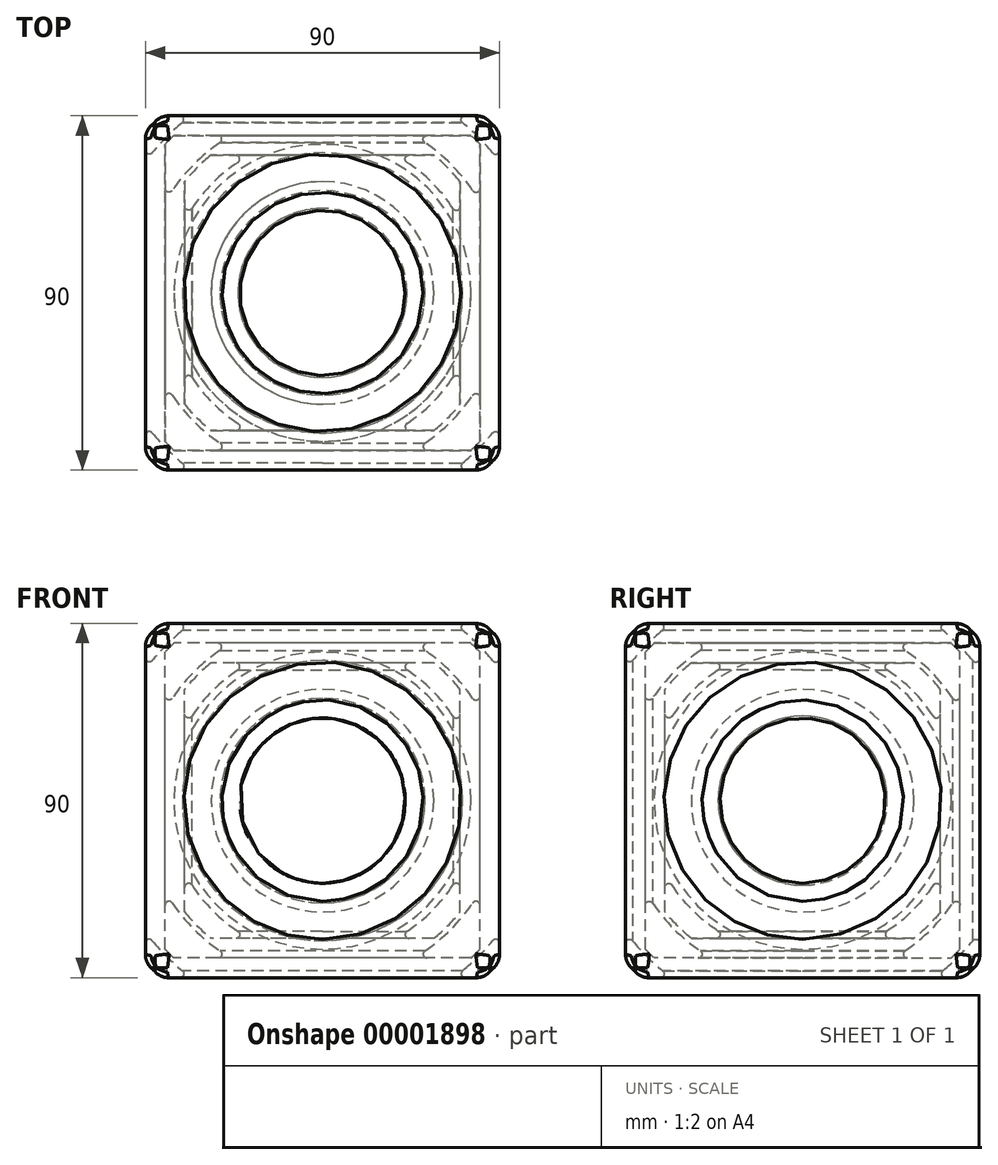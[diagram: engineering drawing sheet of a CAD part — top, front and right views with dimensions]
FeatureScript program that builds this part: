
annotation { "Feature Type Name" : "Feature", "Feature Type Description" : "" }
export const myFeature = defineFeature(function(context is Context, id is Id, definition is map)
    precondition{}
    {
        {
            var Q0;
            Q0=qCreatedBy(makeId("Top.planeOp"),FACE);
            var sketch = newSketch(context, id + "F0", { "sketchPlane" : qUnion([Q0])});
            skLineSegment(sketch, "E0.rect.bottom", {"start": v(35, 35) * mm, "end": v(-35, 35) * mm});
            skLineSegment(sketch, "E0.rect.top", {"start": v(35, -35) * mm, "end": v(-35, -35) * mm});
            skLineSegment(sketch, "E0.rect.left", {"start": v(35, 35) * mm, "end": v(35, -35) * mm});
            skLineSegment(sketch, "E0.rect.right", {"start": v(-35, 35) * mm, "end": v(-35, -35) * mm});
            skPoint(sketch, "E0.rect.middle", {"position": v(0, 0) * mm});
            skSolve(sketch);
        }
        {
            var Q0;
            Q0=qCreatedBy(makeId("Top.planeOp"),FACE);
            var sketch = newSketch(context, id + "F1", { "sketchPlane" : qUnion([Q0])});
            skArc(sketch, "E1", {"start": v(0, 39.5) * mm, "mid": v(-39.5, 0) * mm, "end": v(0, -39.5) * mm});
            skLineSegment(sketch, "E2", {"start": v(0, 39.5) * mm, "end": v(0, -39.5) * mm});
            skSolve(sketch);
        }
        {
            var Q0;
            Q0=makeQuery(id+"F0.imprint","IMPRINT",FACE,{"disambiguationData":[TD([[makeQuery(id+"F0.imprint","IMPRINT",EDGE,{"derivedFrom":sQuery(id+"F0.wireOp",EDGE,"E0.rect.bottom")}),1.0]])]});
            extrude(context, id + "F2", {"entities" : qUnion([Q0]), "endBound" : BoundingType.SYMMETRIC, "depth" : 70 * mm});
        }
        {
            var Q0;
            Q0 = qSketchRegion(id + "F1", true);
            var Q1;
            Q1=sQuery(id+"F1.wireOp",EDGE,"E2");
            revolve(context, id + "F3", {"operationType" : NewBodyOperationType.REMOVE, "entities" : qUnion([Q0]), "axis" : qUnion([Q1]), "revolveType" : RevolveType.FULL, "oppositeDirection" : true});
        }
        {
            var Q0;
            Q0=qCreatedBy(makeId("Top.planeOp"),FACE);
            var sketch = newSketch(context, id + "F4", { "sketchPlane" : qUnion([Q0])});
            skArc(sketch, "E3", {"start": v(0, 45) * mm, "mid": v(-45, 0) * mm, "end": v(0, -45) * mm});
            skLineSegment(sketch, "E4", {"start": v(0, 75) * mm, "end": v(0, -75) * mm});
            skArc(sketch, "E5.0", {"start": v(0, 75) * mm, "mid": v(-75, 0) * mm, "end": v(0, -75) * mm});
            skSolve(sketch);
        }
        {
            var Q0;
            {var subQ2=sQuery(id+"F4.wireOp",EDGE,"E3");Q0=makeQuery(id+"F4.imprint","IMPRINT",FACE,{"disambiguationData":[TD([[makeQuery(id+"F4.imprint","IMPRINT",EDGE,{"derivedFrom":subQ2}),-1.0]])]});}
            var Q1;
            Q1=sQuery(id+"F4.wireOp",EDGE,"E4");
            revolve(context, id + "F5", {"operationType" : NewBodyOperationType.REMOVE, "entities" : qUnion([Q0]), "axis" : qUnion([Q1]), "revolveType" : RevolveType.FULL, "oppositeDirection" : true});
        }
        {
            var Q0;
            Q0=qCreatedBy(makeId("Top.planeOp"),FACE);
            var sketch = newSketch(context, id + "F6", { "sketchPlane" : qUnion([Q0])});
            skLineSegment(sketch, "E6.rect.bottom", {"start": v(40, 40) * mm, "end": v(-40, 40) * mm});
            skLineSegment(sketch, "E6.rect.top", {"start": v(40, -40) * mm, "end": v(-40, -40) * mm});
            skLineSegment(sketch, "E6.rect.left", {"start": v(40, 40) * mm, "end": v(40, -40) * mm});
            skLineSegment(sketch, "E6.rect.right", {"start": v(-40, 40) * mm, "end": v(-40, -40) * mm});
            skPoint(sketch, "E6.rect.middle", {"position": v(0, 0) * mm});
            skSolve(sketch);
        }
        {
            var Q0;
            Q0=qCreatedBy(makeId("Top.planeOp"),FACE);
            var sketch = newSketch(context, id + "F7", { "sketchPlane" : qUnion([Q0])});
            skArc(sketch, "E7", {"start": v(46.2, 0) * mm, "mid": v(0, 46.2) * mm, "end": v(-46.2, 0) * mm});
            skLineSegment(sketch, "E8", {"start": v(-46.2, 0) * mm, "end": v(46.2, 0) * mm});
            skSolve(sketch);
        }
        {
            var Q0;
            Q0=qCreatedBy(makeId("Top.planeOp"),FACE);
            var sketch = newSketch(context, id + "F8", { "sketchPlane" : qUnion([Q0])});
            skArc(sketch, "E9", {"start": v(54.42, 0) * mm, "mid": v(0, 54.42) * mm, "end": v(-54.42, 0) * mm});
            skLineSegment(sketch, "E10", {"start": v(-54.42, 0) * mm, "end": v(54.42, 0) * mm});
            skSolve(sketch);
        }
        {
            var Q0;
            Q0=qCreatedBy(makeId("Top.planeOp"),FACE);
            var sketch = newSketch(context, id + "F9", { "sketchPlane" : qUnion([Q0])});
            skArc(sketch, "E11", {"start": v(55, 0) * mm, "mid": v(0, 55) * mm, "end": v(-55, 0) * mm});
            skLineSegment(sketch, "E12", {"start": v(-111.11, 0) * mm, "end": v(-55, 0) * mm});
            skArc(sketch, "E13.0", {"start": v(111.11, 0) * mm, "mid": v(0, 111.11) * mm, "end": v(-111.11, 0) * mm});
            skLineSegment(sketch, "E14.trimOffspring", {"start": v(55, 0) * mm, "end": v(111.11, 0) * mm});
            skSolve(sketch);
        }
        {
            var Q0;
            Q0=makeQuery(id+"F6.imprint","IMPRINT",FACE,{"disambiguationData":[TD([[makeQuery(id+"F6.imprint","IMPRINT",EDGE,{"derivedFrom":sQuery(id+"F6.wireOp",EDGE,"E6.rect.bottom")}),1.0]])]});
            extrude(context, id + "F10", {"entities" : qUnion([Q0]), "endBound" : BoundingType.SYMMETRIC, "depth" : 80 * mm});
        }
        {
            var Q0;
            Q0 = qSketchRegion(id + "F7", true);
            var Q1;
            Q1=sQuery(id+"F7.wireOp",EDGE,"E7");
            var Q2;
            Q2=sQuery(id+"F8.wireOp",EDGE,"E10");
            revolve(context, id + "F11", {"entities" : qUnion([Q0]), "surfaceEntities" : qUnion([Q1]), "axis" : qUnion([Q2]), "revolveType" : RevolveType.FULL});
        }
        {
            var Q0;
            Q0=makeQuery(id+"F11.opRevolve","SWEPT_BODY",BODY,{"disambiguationData":[OSD([sQuery(id+"F7.wireOp",EDGE,"E7"),sQuery(id+"F7.wireOp",EDGE,"E8")])]});
            var Q1;
            Q1=makeQuery(id+"F10.opExtrude","SWEPT_BODY",BODY,{"disambiguationData":[OSD([sQuery(id+"F6.wireOp",EDGE,"E6.rect.bottom"),sQuery(id+"F6.wireOp",EDGE,"E6.rect.top"),sQuery(id+"F6.wireOp",EDGE,"E6.rect.left"),sQuery(id+"F6.wireOp",EDGE,"E6.rect.right")])]});
            booleanBodies(context, id + "F12", {"operationType" : BooleanOperationType.SUBTRACTION, "tools" : qUnion([Q0]), "targets" : qUnion([Q1])});
        }
        {
            var Q0;
            Q0=makeQuery(id+"F9.imprint","IMPRINT",FACE,{"disambiguationData":[TD([[makeQuery(id+"F9.imprint","IMPRINT",EDGE,{"derivedFrom":sQuery(id+"F9.wireOp",EDGE,"E11")}),-1.0]])]});
            var Q1;
            Q1=sQuery(id+"F9.wireOp",EDGE,"E12");
            revolve(context, id + "F13", {"operationType" : NewBodyOperationType.REMOVE, "entities" : qUnion([Q0]), "axis" : qUnion([Q1]), "revolveType" : RevolveType.FULL, "oppositeDirection" : true});
        }
        {
            var Q0;
            Q0=makeQuery(id+"F12.opBoolean","INTERSECT",EDGE,{"derivedFrom":[makeQuery(id+"F10.opExtrude","CAP_FACE",FACE,{"disambiguationData":[OSD([sQuery(id+"F6.wireOp",EDGE,"E6.rect.bottom"),sQuery(id+"F6.wireOp",EDGE,"E6.rect.top"),sQuery(id+"F6.wireOp",EDGE,"E6.rect.left"),sQuery(id+"F6.wireOp",EDGE,"E6.rect.right")])],"isStart":true}),makeQuery(id+"F11.opRevolve","SWEPT_FACE",FACE,{"disambiguationData":[OSD([sQuery(id+"F7.wireOp",EDGE,"E7")])]})]});
            var Q1;
            Q1=makeQuery(id+"F12.opBoolean","INTERSECT",EDGE,{"derivedFrom":[makeQuery(id+"F10.opExtrude","SWEPT_FACE",FACE,{"disambiguationData":[OSD([sQuery(id+"F6.wireOp",EDGE,"E6.rect.bottom")])]}),makeQuery(id+"F11.opRevolve","SWEPT_FACE",FACE,{"disambiguationData":[OSD([sQuery(id+"F7.wireOp",EDGE,"E7")])]})]});
            var Q2;
            Q2=makeQuery(id+"F12.opBoolean","INTERSECT",EDGE,{"derivedFrom":[makeQuery(id+"F10.opExtrude","SWEPT_FACE",FACE,{"disambiguationData":[OSD([sQuery(id+"F6.wireOp",EDGE,"E6.rect.left")])]}),makeQuery(id+"F11.opRevolve","SWEPT_FACE",FACE,{"disambiguationData":[OSD([sQuery(id+"F7.wireOp",EDGE,"E7")])]})]});
            var Q3;
            Q3=makeQuery(id+"F12.opBoolean","INTERSECT",EDGE,{"derivedFrom":[makeQuery(id+"F10.opExtrude","SWEPT_FACE",FACE,{"disambiguationData":[OSD([sQuery(id+"F6.wireOp",EDGE,"E6.rect.right")])]}),makeQuery(id+"F11.opRevolve","SWEPT_FACE",FACE,{"disambiguationData":[OSD([sQuery(id+"F7.wireOp",EDGE,"E7")])]})]});
            var Q4;
            Q4=makeQuery(id+"F12.opBoolean","INTERSECT",EDGE,{"derivedFrom":[makeQuery(id+"F10.opExtrude","SWEPT_FACE",FACE,{"disambiguationData":[OSD([sQuery(id+"F6.wireOp",EDGE,"E6.rect.top")])]}),makeQuery(id+"F11.opRevolve","SWEPT_FACE",FACE,{"disambiguationData":[OSD([sQuery(id+"F7.wireOp",EDGE,"E7")])]})]});
            var Q5;
            Q5=makeQuery(id+"F12.opBoolean","INTERSECT",EDGE,{"derivedFrom":[makeQuery(id+"F10.opExtrude","CAP_FACE",FACE,{"disambiguationData":[OSD([sQuery(id+"F6.wireOp",EDGE,"E6.rect.bottom"),sQuery(id+"F6.wireOp",EDGE,"E6.rect.top"),sQuery(id+"F6.wireOp",EDGE,"E6.rect.left"),sQuery(id+"F6.wireOp",EDGE,"E6.rect.right")])],"isStart":false}),makeQuery(id+"F11.opRevolve","SWEPT_FACE",FACE,{"disambiguationData":[OSD([sQuery(id+"F7.wireOp",EDGE,"E7")])]})]});
            fillet(context, id + "F14", {"entities" : qUnion([Q0, Q1, Q2, Q3, Q4, Q5]), "radius" : 1 * mm, "tangentPropagation" : true, "allowEdgeOverflow" : false});
        }
        {
            var Q0;
            Q0=makeQuery(id+"F3.boolean.opBoolean","INTERSECT",EDGE,{"derivedFrom":[makeQuery(id+"F2.opExtrude","CAP_FACE",FACE,{"disambiguationData":[OSD([sQuery(id+"F0.wireOp",EDGE,"E0.rect.bottom"),sQuery(id+"F0.wireOp",EDGE,"E0.rect.top"),sQuery(id+"F0.wireOp",EDGE,"E0.rect.left"),sQuery(id+"F0.wireOp",EDGE,"E0.rect.right")])],"isStart":false}),makeQuery(id+"F3.opRevolve","SWEPT_FACE",FACE,{"disambiguationData":[OSD([sQuery(id+"F1.wireOp",EDGE,"E1")])]})]});
            var Q1;
            Q1=makeQuery(id+"F3.boolean.opBoolean","INTERSECT",EDGE,{"derivedFrom":[makeQuery(id+"F2.opExtrude","SWEPT_FACE",FACE,{"disambiguationData":[OSD([sQuery(id+"F0.wireOp",EDGE,"E0.rect.top")])]}),makeQuery(id+"F3.opRevolve","SWEPT_FACE",FACE,{"disambiguationData":[OSD([sQuery(id+"F1.wireOp",EDGE,"E1")])]})]});
            var Q2;
            Q2=makeQuery(id+"F3.boolean.opBoolean","INTERSECT",EDGE,{"derivedFrom":[makeQuery(id+"F2.opExtrude","CAP_FACE",FACE,{"disambiguationData":[OSD([sQuery(id+"F0.wireOp",EDGE,"E0.rect.bottom"),sQuery(id+"F0.wireOp",EDGE,"E0.rect.top"),sQuery(id+"F0.wireOp",EDGE,"E0.rect.left"),sQuery(id+"F0.wireOp",EDGE,"E0.rect.right")])],"isStart":true}),makeQuery(id+"F3.opRevolve","SWEPT_FACE",FACE,{"disambiguationData":[OSD([sQuery(id+"F1.wireOp",EDGE,"E1")])]})]});
            var Q3;
            Q3=makeQuery(id+"F3.boolean.opBoolean","INTERSECT",EDGE,{"derivedFrom":[makeQuery(id+"F2.opExtrude","SWEPT_FACE",FACE,{"disambiguationData":[OSD([sQuery(id+"F0.wireOp",EDGE,"E0.rect.left")])]}),makeQuery(id+"F3.opRevolve","SWEPT_FACE",FACE,{"disambiguationData":[OSD([sQuery(id+"F1.wireOp",EDGE,"E1")])]})]});
            var Q4;
            Q4=makeQuery(id+"F3.boolean.opBoolean","INTERSECT",EDGE,{"derivedFrom":[makeQuery(id+"F2.opExtrude","SWEPT_FACE",FACE,{"disambiguationData":[OSD([sQuery(id+"F0.wireOp",EDGE,"E0.rect.bottom")])]}),makeQuery(id+"F3.opRevolve","SWEPT_FACE",FACE,{"disambiguationData":[OSD([sQuery(id+"F1.wireOp",EDGE,"E1")])]})]});
            var Q5;
            Q5=makeQuery(id+"F3.boolean.opBoolean","INTERSECT",EDGE,{"derivedFrom":[makeQuery(id+"F2.opExtrude","SWEPT_FACE",FACE,{"disambiguationData":[OSD([sQuery(id+"F0.wireOp",EDGE,"E0.rect.right")])]}),makeQuery(id+"F3.opRevolve","SWEPT_FACE",FACE,{"disambiguationData":[OSD([sQuery(id+"F1.wireOp",EDGE,"E1")])]})]});
            fillet(context, id + "F15", {"entities" : qUnion([Q0, Q1, Q2, Q3, Q4, Q5]), "radius" : 1 * mm, "tangentPropagation" : true, "allowEdgeOverflow" : false});
        }
        {
            var Q0;
            Q0=makeQuery(id+"F2.opExtrude","CAP_FACE",FACE,{"disambiguationData":[OSD([sQuery(id+"F0.wireOp",EDGE,"E0.rect.bottom"),sQuery(id+"F0.wireOp",EDGE,"E0.rect.top"),sQuery(id+"F0.wireOp",EDGE,"E0.rect.left"),sQuery(id+"F0.wireOp",EDGE,"E0.rect.right")])],"isStart":true});
            var sketch = newSketch(context, id + "F16", { "sketchPlane" : qUnion([Q0])});
            skCircle(sketch, "E15", {"center": v(0, 0) * mm, "radius": 24 * mm});
            skCircle(sketch, "E16.0", {"center": v(0, 0) * mm, "radius": 23.6 * mm});
            skSolve(sketch);
        }
        {
            var Q0;
            Q0=qCreatedBy(makeId("Top.planeOp"),FACE);
            var sketch = newSketch(context, id + "F17", { "sketchPlane" : qUnion([Q0])});
            skLineSegment(sketch, "E17.rect.bottom", {"start": v(45, 45) * mm, "end": v(-45, 45) * mm});
            skLineSegment(sketch, "E17.rect.top", {"start": v(45, -45) * mm, "end": v(-45, -45) * mm});
            skLineSegment(sketch, "E17.rect.left", {"start": v(45, 45) * mm, "end": v(45, -45) * mm});
            skLineSegment(sketch, "E17.rect.right", {"start": v(-45, 45) * mm, "end": v(-45, -45) * mm});
            skPoint(sketch, "E17.rect.middle", {"position": v(0, 0) * mm});
            skSolve(sketch);
        }
        {
            var Q0;
            Q0=qCreatedBy(makeId("Top.planeOp"),FACE);
            var sketch = newSketch(context, id + "F18", { "sketchPlane" : qUnion([Q0])});
            skArc(sketch, "E18", {"start": v(56, 0) * mm, "mid": v(0, 56) * mm, "end": v(-56, 0) * mm});
            skLineSegment(sketch, "E19", {"start": v(-56, 0) * mm, "end": v(56, 0) * mm});
            skSolve(sketch);
        }
        {
            var Q0;
            Q0=makeQuery(id+"F17.imprint","IMPRINT",FACE,{"disambiguationData":[TD([[makeQuery(id+"F17.imprint","IMPRINT",EDGE,{"derivedFrom":sQuery(id+"F17.wireOp",EDGE,"E17.rect.bottom")}),1.0]])]});
            var Q1;
            Q1 = qSketchRegion(id + "F16", true);
            extrude(context, id + "F19", {"entities" : qUnion([Q0, Q1]), "endBound" : BoundingType.SYMMETRIC, "depth" : 90 * mm});
        }
        {
            var Q0;
            Q0 = qSketchRegion(id + "F18", true);
            var Q1;
            Q1=sQuery(id+"F18.wireOp",EDGE,"E19");
            revolve(context, id + "F20", {"entities" : qUnion([Q0]), "axis" : qUnion([Q1]), "revolveType" : RevolveType.FULL});
        }
        {
            var Q0;
            Q0=makeQuery(id+"F20.opRevolve","SWEPT_BODY",BODY,{"disambiguationData":[OSD([sQuery(id+"F18.wireOp",EDGE,"E18"),sQuery(id+"F18.wireOp",EDGE,"E19")])]});
            var Q1;
            Q1=makeQuery(id+"F19.opExtrude","SWEPT_BODY",BODY,{"disambiguationData":[OSD([sQuery(id+"F17.wireOp",EDGE,"E17.rect.bottom"),sQuery(id+"F17.wireOp",EDGE,"E17.rect.top"),sQuery(id+"F17.wireOp",EDGE,"E17.rect.left"),sQuery(id+"F17.wireOp",EDGE,"E17.rect.right")])]});
            booleanBodies(context, id + "F21", {"operationType" : BooleanOperationType.SUBTRACTION, "tools" : qUnion([Q0]), "targets" : qUnion([Q1])});
        }
        {
            var Q0;
            Q0=makeQuery(id+"F19.opExtrude","SWEPT_BODY",BODY,{"disambiguationData":[OSD([sQuery(id+"F16.wireOp",EDGE,"E15")])]});
            deleteBodies(context, id + "F22", {"entities" : qUnion([Q0])});
        }
        {
            var Q0;
            Q0=makeQuery(id+"F19.opExtrude","CAP_EDGE",EDGE,{"disambiguationData":[OSD([sQuery(id+"F17.wireOp",EDGE,"E17.rect.left")])],"isStart":false});
            var Q1;
            Q1=makeQuery(id+"F19.opExtrude","CAP_EDGE",EDGE,{"disambiguationData":[OSD([sQuery(id+"F17.wireOp",EDGE,"E17.rect.bottom")])],"isStart":false});
            var Q2;
            Q2=makeQuery(id+"F19.opExtrude","SWEPT_EDGE",EDGE,{"disambiguationData":[OSD([sQuery(id+"F17.wireOp",EDGE,"E17.rect.bottom"),sQuery(id+"F17.wireOp",EDGE,"E17.rect.left")])]});
            var Q3;
            Q3=makeQuery(id+"F19.opExtrude","SWEPT_EDGE",EDGE,{"disambiguationData":[OSD([sQuery(id+"F17.wireOp",EDGE,"E17.rect.bottom"),sQuery(id+"F17.wireOp",EDGE,"E17.rect.right")])]});
            var Q4;
            Q4=makeQuery(id+"F19.opExtrude","CAP_EDGE",EDGE,{"disambiguationData":[OSD([sQuery(id+"F17.wireOp",EDGE,"E17.rect.right")])],"isStart":false});
            var Q5;
            Q5=makeQuery(id+"F19.opExtrude","SWEPT_EDGE",EDGE,{"disambiguationData":[OSD([sQuery(id+"F17.wireOp",EDGE,"E17.rect.top"),sQuery(id+"F17.wireOp",EDGE,"E17.rect.right")])]});
            var Q6;
            Q6=makeQuery(id+"F19.opExtrude","CAP_EDGE",EDGE,{"disambiguationData":[OSD([sQuery(id+"F17.wireOp",EDGE,"E17.rect.top")])],"isStart":false});
            var Q7;
            Q7=makeQuery(id+"F19.opExtrude","SWEPT_EDGE",EDGE,{"disambiguationData":[OSD([sQuery(id+"F17.wireOp",EDGE,"E17.rect.top"),sQuery(id+"F17.wireOp",EDGE,"E17.rect.left")])]});
            var Q8;
            Q8=makeQuery(id+"F19.opExtrude","CAP_EDGE",EDGE,{"disambiguationData":[OSD([sQuery(id+"F17.wireOp",EDGE,"E17.rect.left")])],"isStart":true});
            var Q9;
            Q9=makeQuery(id+"F19.opExtrude","CAP_EDGE",EDGE,{"disambiguationData":[OSD([sQuery(id+"F17.wireOp",EDGE,"E17.rect.bottom")])],"isStart":true});
            var Q10;
            Q10=makeQuery(id+"F19.opExtrude","CAP_EDGE",EDGE,{"disambiguationData":[OSD([sQuery(id+"F17.wireOp",EDGE,"E17.rect.right")])],"isStart":true});
            var Q11;
            Q11=makeQuery(id+"F19.opExtrude","CAP_EDGE",EDGE,{"disambiguationData":[OSD([sQuery(id+"F17.wireOp",EDGE,"E17.rect.top")])],"isStart":true});
            chamfer(context, id + "F23", {"entities" : qUnion([Q0, Q1, Q2, Q3, Q4, Q5, Q6, Q7, Q8, Q9, Q10, Q11]), "width" : 4 * mm, "tangentPropagation" : true});
        }
        {
            var Q0;
            Q0=makeQuery(id+"F21.opBoolean","INTERSECT",EDGE,{"derivedFrom":[makeQuery(id+"F19.opExtrude","SWEPT_FACE",FACE,{"disambiguationData":[OSD([sQuery(id+"F17.wireOp",EDGE,"E17.rect.bottom")])]}),makeQuery(id+"F20.opRevolve","SWEPT_FACE",FACE,{"disambiguationData":[OSD([sQuery(id+"F18.wireOp",EDGE,"E18")])]})]});
            var Q1;
            Q1=makeQuery(id+"F21.opBoolean","INTERSECT",EDGE,{"derivedFrom":[makeQuery(id+"F19.opExtrude","CAP_FACE",FACE,{"disambiguationData":[OSD([sQuery(id+"F17.wireOp",EDGE,"E17.rect.bottom"),sQuery(id+"F17.wireOp",EDGE,"E17.rect.top"),sQuery(id+"F17.wireOp",EDGE,"E17.rect.left"),sQuery(id+"F17.wireOp",EDGE,"E17.rect.right")])],"isStart":false}),makeQuery(id+"F20.opRevolve","SWEPT_FACE",FACE,{"disambiguationData":[OSD([sQuery(id+"F18.wireOp",EDGE,"E18")])]})]});
            var Q2;
            Q2=makeQuery(id+"F21.opBoolean","INTERSECT",EDGE,{"derivedFrom":[makeQuery(id+"F19.opExtrude","SWEPT_FACE",FACE,{"disambiguationData":[OSD([sQuery(id+"F17.wireOp",EDGE,"E17.rect.right")])]}),makeQuery(id+"F20.opRevolve","SWEPT_FACE",FACE,{"disambiguationData":[OSD([sQuery(id+"F18.wireOp",EDGE,"E18")])]})]});
            var Q3;
            Q3=makeQuery(id+"F21.opBoolean","INTERSECT",EDGE,{"derivedFrom":[makeQuery(id+"F19.opExtrude","SWEPT_FACE",FACE,{"disambiguationData":[OSD([sQuery(id+"F17.wireOp",EDGE,"E17.rect.top")])]}),makeQuery(id+"F20.opRevolve","SWEPT_FACE",FACE,{"disambiguationData":[OSD([sQuery(id+"F18.wireOp",EDGE,"E18")])]})]});
            var Q4;
            Q4=makeQuery(id+"F21.opBoolean","INTERSECT",EDGE,{"derivedFrom":[makeQuery(id+"F19.opExtrude","CAP_FACE",FACE,{"disambiguationData":[OSD([sQuery(id+"F17.wireOp",EDGE,"E17.rect.bottom"),sQuery(id+"F17.wireOp",EDGE,"E17.rect.top"),sQuery(id+"F17.wireOp",EDGE,"E17.rect.left"),sQuery(id+"F17.wireOp",EDGE,"E17.rect.right")])],"isStart":true}),makeQuery(id+"F20.opRevolve","SWEPT_FACE",FACE,{"disambiguationData":[OSD([sQuery(id+"F18.wireOp",EDGE,"E18")])]})]});
            var Q5;
            Q5=makeQuery(id+"F21.opBoolean","INTERSECT",EDGE,{"derivedFrom":[makeQuery(id+"F19.opExtrude","SWEPT_FACE",FACE,{"disambiguationData":[OSD([sQuery(id+"F17.wireOp",EDGE,"E17.rect.left")])]}),makeQuery(id+"F20.opRevolve","SWEPT_FACE",FACE,{"disambiguationData":[OSD([sQuery(id+"F18.wireOp",EDGE,"E18")])]})]});
            fillet(context, id + "F24", {"entities" : qUnion([Q0, Q1, Q2, Q3, Q4, Q5]), "radius" : 1 * mm, "tangentPropagation" : true, "allowEdgeOverflow" : false});
        }
        {
            var Q0;
            Q0=qCreatedBy(makeId("Top.planeOp"),FACE);
            var sketch = newSketch(context, id + "F25", { "sketchPlane" : qUnion([Q0])});
            skLineSegment(sketch, "E20.rect.bottom", {"start": v(50, 50) * mm, "end": v(-50, 50) * mm});
            skLineSegment(sketch, "E20.rect.top", {"start": v(50, -50) * mm, "end": v(-50, -50) * mm});
            skLineSegment(sketch, "E20.rect.left", {"start": v(50, 50) * mm, "end": v(50, -50) * mm});
            skLineSegment(sketch, "E20.rect.right", {"start": v(-50, 50) * mm, "end": v(-50, -50) * mm});
            skPoint(sketch, "E20.rect.middle", {"position": v(0, 0) * mm});
            skSolve(sketch);
        }
        {
            var Q0;
            {var subQ0=sQuery(id+"F17.wireOp",EDGE,"E17.rect.right");Q0=makeQuery(id+"F23.opChamfer","BLEND_FACE",FACE,{"disambiguationData":[OSD([subQ0]),TDD([makeQuery(id+"F19.opExtrude","CAP_EDGE",EDGE,{"disambiguationData":[OSD([subQ0])],"isStart":false})])]});}
            var Q1;
            {var subQ0=sQuery(id+"F17.wireOp",EDGE,"E17.rect.top");Q1=makeQuery(id+"F23.opChamfer","BLEND_FACE",FACE,{"disambiguationData":[OSD([subQ0]),TDD([makeQuery(id+"F19.opExtrude","CAP_EDGE",EDGE,{"disambiguationData":[OSD([subQ0])],"isStart":false})])]});}
            var Q2;
            {var subQ0=sQuery(id+"F17.wireOp",EDGE,"E17.rect.top");var subQ1=sQuery(id+"F17.wireOp",EDGE,"E17.rect.right");Q2=makeQuery(id+"F23.opChamfer","BLEND_FACE",FACE,{"disambiguationData":[OSD([subQ0,subQ1]),TDD([makeQuery(id+"F19.opExtrude","SWEPT_EDGE",EDGE,{"disambiguationData":[OSD([subQ0,subQ1])]})])]});}
            var Q3;
            {var subQ0=sQuery(id+"F17.wireOp",EDGE,"E17.rect.top");var subQ1=sQuery(id+"F17.wireOp",EDGE,"E17.rect.left");Q3=makeQuery(id+"F23.opChamfer","BLEND_FACE",FACE,{"disambiguationData":[OSD([subQ0,subQ1]),TDD([makeQuery(id+"F19.opExtrude","SWEPT_EDGE",EDGE,{"disambiguationData":[OSD([subQ0,subQ1])]})])]});}
            var Q4;
            {var subQ0=sQuery(id+"F17.wireOp",EDGE,"E17.rect.left");Q4=makeQuery(id+"F23.opChamfer","BLEND_FACE",FACE,{"disambiguationData":[OSD([subQ0]),TDD([makeQuery(id+"F19.opExtrude","CAP_EDGE",EDGE,{"disambiguationData":[OSD([subQ0])],"isStart":false})])]});}
            var Q5;
            {var subQ0=sQuery(id+"F17.wireOp",EDGE,"E17.rect.top");Q5=makeQuery(id+"F23.opChamfer","BLEND_FACE",FACE,{"disambiguationData":[OSD([subQ0]),TDD([makeQuery(id+"F19.opExtrude","CAP_EDGE",EDGE,{"disambiguationData":[OSD([subQ0])],"isStart":true})])]});}
            var Q6;
            {var subQ0=sQuery(id+"F17.wireOp",EDGE,"E17.rect.left");Q6=makeQuery(id+"F23.opChamfer","BLEND_FACE",FACE,{"disambiguationData":[OSD([subQ0]),TDD([makeQuery(id+"F19.opExtrude","CAP_EDGE",EDGE,{"disambiguationData":[OSD([subQ0])],"isStart":true})])]});}
            var Q7;
            {var subQ0=sQuery(id+"F17.wireOp",EDGE,"E17.rect.bottom");var subQ1=sQuery(id+"F17.wireOp",EDGE,"E17.rect.left");Q7=makeQuery(id+"F23.opChamfer","BLEND_FACE",FACE,{"disambiguationData":[OSD([subQ0,subQ1]),TDD([makeQuery(id+"F19.opExtrude","SWEPT_EDGE",EDGE,{"disambiguationData":[OSD([subQ0,subQ1])]})])]});}
            var Q8;
            {var subQ0=sQuery(id+"F17.wireOp",EDGE,"E17.rect.bottom");Q8=makeQuery(id+"F23.opChamfer","BLEND_FACE",FACE,{"disambiguationData":[OSD([subQ0]),TDD([makeQuery(id+"F19.opExtrude","CAP_EDGE",EDGE,{"disambiguationData":[OSD([subQ0])],"isStart":true})])]});}
            var Q9;
            {var subQ0=sQuery(id+"F17.wireOp",EDGE,"E17.rect.bottom");Q9=makeQuery(id+"F23.opChamfer","BLEND_FACE",FACE,{"disambiguationData":[OSD([subQ0]),TDD([makeQuery(id+"F19.opExtrude","CAP_EDGE",EDGE,{"disambiguationData":[OSD([subQ0])],"isStart":false})])]});}
            var Q10;
            {var subQ0=sQuery(id+"F17.wireOp",EDGE,"E17.rect.bottom");var subQ1=sQuery(id+"F17.wireOp",EDGE,"E17.rect.right");Q10=makeQuery(id+"F23.opChamfer","BLEND_FACE",FACE,{"disambiguationData":[OSD([subQ0,subQ1]),TDD([makeQuery(id+"F19.opExtrude","SWEPT_EDGE",EDGE,{"disambiguationData":[OSD([subQ0,subQ1])]})])]});}
            var Q11;
            {var subQ0=sQuery(id+"F17.wireOp",EDGE,"E17.rect.right");Q11=makeQuery(id+"F23.opChamfer","BLEND_FACE",FACE,{"disambiguationData":[OSD([subQ0]),TDD([makeQuery(id+"F19.opExtrude","CAP_EDGE",EDGE,{"disambiguationData":[OSD([subQ0])],"isStart":true})])]});}
            fillet(context, id + "F26", {"entities" : qUnion([Q0, Q1, Q2, Q3, Q4, Q5, Q6, Q7, Q8, Q9, Q10, Q11]), "radius" : 5 * mm, "tangentPropagation" : true, "rho" : 0.5, "crossSection" : FilletCrossSection.CONIC, "allowEdgeOverflow" : false});
        }
    });
